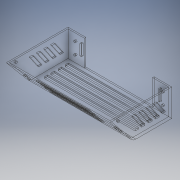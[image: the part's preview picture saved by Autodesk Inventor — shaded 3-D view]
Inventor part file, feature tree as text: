
AUTODESK INVENTOR PART (.ipt)
format: ipt  version: 2018.2 (Build 222227000, 227)  size: 344,576 bytes
history: native  units: mm
features: extrude x12, sketch x11, plane x1, fillet x1
ambient origin geometry x8: Origin, YZ Plane, XZ Plane, XY Plane, X Axis, Y Axis, Z Axis, Center Point
bodies: Solid1 (feature_tree)
feature tree (25):
  extrude  "Extrusion1"  Depth=60.0mm
  extrude  "Extrusion2"  Depth=5.0mm
  extrude  "Extrusion3"  Depth=5.0mm
  extrude  "Extrusion4"  Depth=2.4mm TaperAngle=0.0deg
  extrude  "Extrusion5"  Depth=2.4mm
  sketch  "Sketch6"  dims[d11=39.6mm d12=0.0mm d13=24.43461mm]
  plane  "Work Plane1"
  extrude  "Extrusion8"  Depth=39.6mm
  extrude  "Extrusion9"  Depth=2.4mm TaperAngle=0.0deg
  extrude  "Extrusion10"  Depth=157.6mm TaperAngle=0.0deg
  extrude  "Extrusion11"  Depth=5.0mm
  extrude  "Extrusion12"  Depth=5.0mm
  sketch  "Sketch11"  dims[d25=5.0mm d26=6.0mm d27=5.0mm d28=22.0mm d29=5.0mm d30=6.0mm d31=5.0mm d32=6.0mm d33=5.0mm d34=6.0mm d35=5.0mm d36=10.0mm d39=-50.0mm d40=4.0mm d41=4.0mm d42=10.0mm d43=10.0mm d44=20.0mm d45=20.0mm d46=40.0mm d47=4.0mm d49=4.0mm d50=4.0mm d51=4.0mm d52=4.0mm d55=4.0mm d56=80.0mm d57=80.0mm d58=80.0mm d59=80.000202mm d60=80.0mm d61=160.0mm d62=0.0mm d63=4.0mm d64=10.0mm d65=4.0mm d66=10.0mm d67=17.0mm d68=17.0mm d69=160.0mm d70=0.0mm d71=2.4mm d72=25.0mm d73=0.0mm d74=2.4mm d75=25.0mm d76=0.0mm d77=3.0mm d78=7.0mm d79=5.0mm d80=160.0mm d81=0.0mm d82=3.0mm d83=12.5mm d84=12.0mm d85=3.0mm d86=12.5mm d87=12.0mm d88=3.0mm d89=3.0mm d90=12.5mm d91=12.0mm d92=12.0mm d93=12.5mm d94=12.0mm d95=0.0mm d96=7.0mm d97=2.0mm d98=12.5mm d99=12.5mm d101=2.0mm d103=7.0mm d104=12.5mm d105=3.0mm d106=0.0mm d107=12.5mm d108=10.0mm]
  extrude  "Extrusion13"  Depth=10.0mm
  extrude  "Extrusion14"  Depth=5.0mm
  fillet  "Fillet1"  Radius=22.0mm
  sketch  "Sketch1"  dims[d0=160.0mm d1=60.0mm]
  sketch  "Sketch2"  dims[d2=140.0mm d3=5.0mm]
  sketch  "Sketch3"  dims[d4=5.0mm d5=5.0mm]
  sketch  "Sketch4"  dims[d6=5.0mm d7=2.4mm d8=0.0mm]
  sketch  "Sketch5"  dims[d9=2.4mm d10=2.4mm]
  sketch  "Sketch7"  dims[d14=2.4mm d15=0.0mm d16=2.4mm d17=0.0mm]
  sketch  "Sketch8"  dims[d18=2.4mm d19=157.6mm d20=0.0mm]
  sketch  "Sketch9"  dims[d21=5.0mm d22=6.0mm]
  sketch  "Sketch10"  dims[d23=5.0mm d24=6.0mm]
